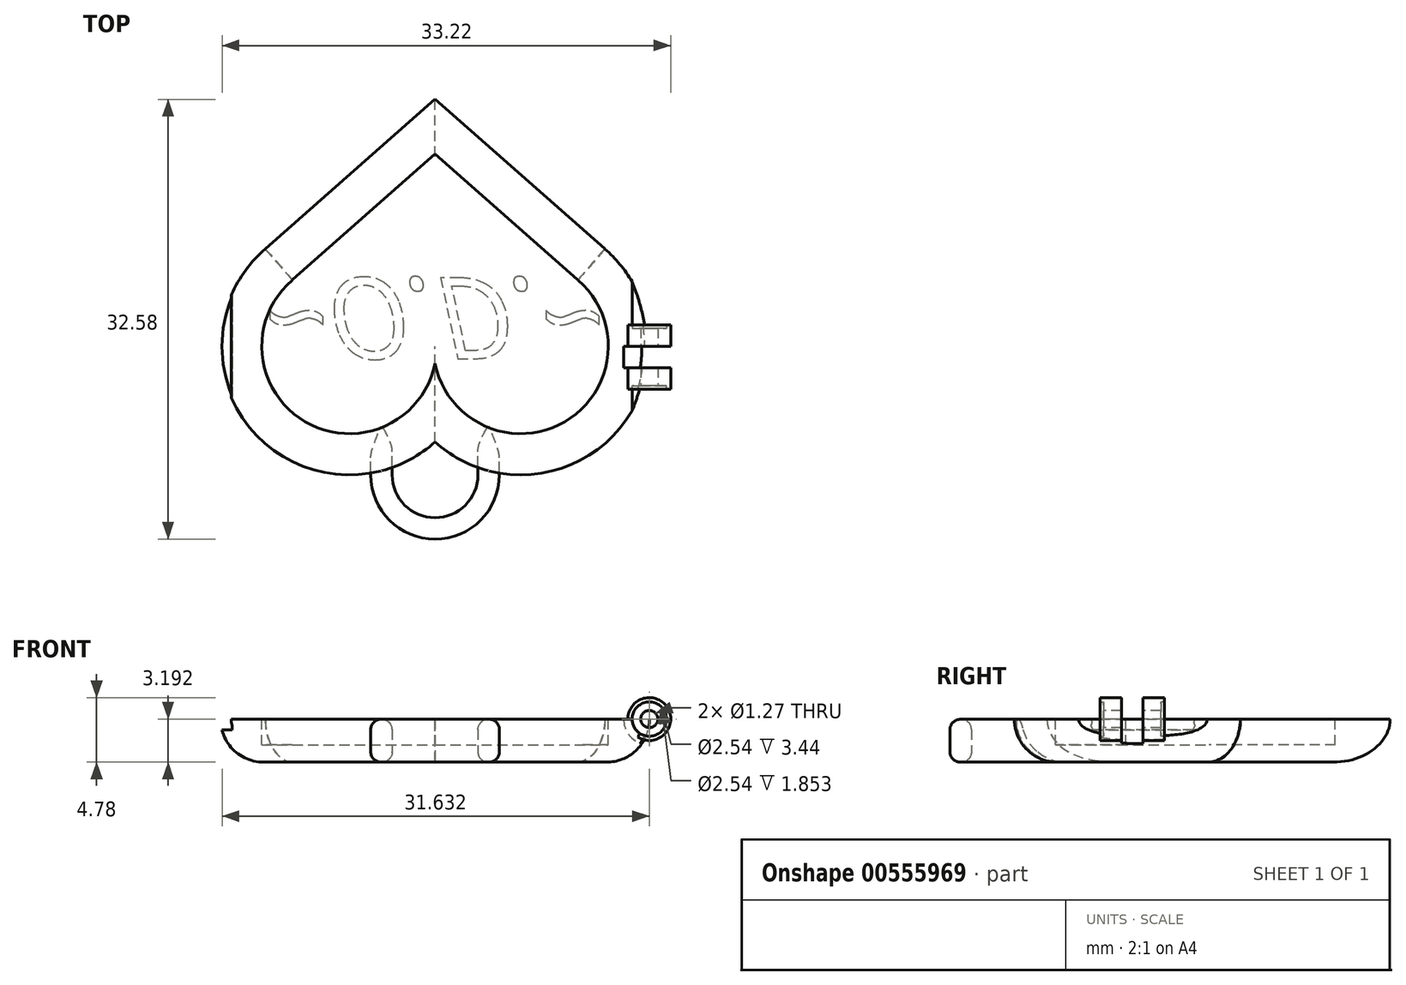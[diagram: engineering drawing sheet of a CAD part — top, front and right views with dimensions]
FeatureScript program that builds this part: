
annotation { "Feature Type Name" : "Feature", "Feature Type Description" : "" }
export const myFeature = defineFeature(function(context is Context, id is Id, definition is map)
    precondition{}
    {
        {
            var Q0;
            Q0=qCreatedBy(makeId("Top.planeOp"),FACE);
            var sketch = newSketch(context, id + "F0", { "sketchPlane" : qUnion([Q0])});
            skArc(sketch, "E0", {"start": v(0, 7.1) * mm, "mid": v(-13.5, 6.29) * mm, "end": v(-12.57, -7.21) * mm});
            skArc(sketch, "E1", {"start": v(0, 7.1) * mm, "mid": v(13.5, 6.29) * mm, "end": v(12.57, -7.21) * mm});
            skLineSegment(sketch, "E2", {"start": v(-12.57, -7.21) * mm, "end": v(0, -18.3) * mm});
            skLineSegment(sketch, "E3", {"start": v(0, -18.3) * mm, "end": v(12.57, -7.21) * mm});
            skSolve(sketch);
        }
        {
            var Q0;
            Q0=makeQuery(id+"F0.imprint","IMPRINT",FACE,{"disambiguationData":[TD([[makeQuery(id+"F0.imprint","IMPRINT",EDGE,{"derivedFrom":sQuery(id+"F0.wireOp",EDGE,"E0")}),1.0]])]});
            extrude(context, id + "F1", {"entities" : qUnion([Q0]), "depth" : 6.35 * mm});
        }
        {
            var Q0;
            Q0=makeQuery(id+"F1.opExtrude","CAP_FACE",FACE,{"disambiguationData":[OSD([sQuery(id+"F0.wireOp",EDGE,"E0"),sQuery(id+"F0.wireOp",EDGE,"E1"),sQuery(id+"F0.wireOp",EDGE,"E2"),sQuery(id+"F0.wireOp",EDGE,"E3")])],"isStart":false});
            var Q1;
            Q1=makeQuery(id+"F1.opExtrude","CAP_FACE",FACE,{"disambiguationData":[OSD([sQuery(id+"F0.wireOp",EDGE,"E0"),sQuery(id+"F0.wireOp",EDGE,"E1"),sQuery(id+"F0.wireOp",EDGE,"E2"),sQuery(id+"F0.wireOp",EDGE,"E3")])],"isStart":true});
            fillet(context, id + "F2", {"entities" : qUnion([Q0, Q1]), "radius" : 3.17 * mm, "tangentPropagation" : true, "allowEdgeOverflow" : false});
        }
        {
            var Q0;
            Q0=makeQuery(id+"F2.opFillet","BLEND_EDGE",EDGE,{"blendedFrom":[makeQuery(id+"F1.opExtrude","CAP_EDGE",EDGE,{"disambiguationData":[OSD([sQuery(id+"F0.wireOp",EDGE,"E0")])],"isStart":false}),makeQuery(id+"F1.opExtrude","CAP_EDGE",EDGE,{"disambiguationData":[OSD([sQuery(id+"F0.wireOp",EDGE,"E2")])],"isStart":false})],"blendedInto":[]});
            var Q1;
            Q1=makeQuery(id+"F2.opFillet","BLEND_EDGE",EDGE,{"blendedFrom":[makeQuery(id+"F1.opExtrude","CAP_EDGE",EDGE,{"disambiguationData":[OSD([sQuery(id+"F0.wireOp",EDGE,"E1")])],"isStart":false}),makeQuery(id+"F1.opExtrude","CAP_EDGE",EDGE,{"disambiguationData":[OSD([sQuery(id+"F0.wireOp",EDGE,"E3")])],"isStart":false})],"blendedInto":[]});
            fillet(context, id + "F3", {"entities" : qUnion([Q0, Q1]), "radius" : 2.54 * mm, "tangentPropagation" : true, "allowEdgeOverflow" : false});
        }
        {
            var Q0;
            Q0=qCreatedBy(makeId("Top.planeOp"),FACE);
            var sketch = newSketch(context, id + "F4", { "sketchPlane" : qUnion([Q0])});
            skCircle(sketch, "E4", {"center": v(0, 9.53) * mm, "radius": 3.18 * mm});
            skCircle(sketch, "E5", {"center": v(0, 9.53) * mm, "radius": 4.76 * mm});
            skLineSegment(sketch, "E6", {"start": v(-4.76, 9.53) * mm, "end": v(-4.76, 0) * mm});
            skLineSegment(sketch, "E7", {"start": v(4.76, 9.53) * mm, "end": v(4.76, 0) * mm});
            skLineSegment(sketch, "E8", {"start": v(3.18, 9.53) * mm, "end": v(3.18, 0) * mm});
            skLineSegment(sketch, "E9", {"start": v(-3.17, 9.53) * mm, "end": v(-3.17, 0) * mm});
            skLineSegment(sketch, "E10", {"start": v(-4.76, 0) * mm, "end": v(4.76, 0) * mm});
            skSolve(sketch);
        }
        {
            var Q0;
            {var subQ5=sQuery(id+"F4.wireOp",EDGE,"E8");var subQ7=sQuery(id+"F4.wireOp",EDGE,"E4");var subQ8=makeQuery(id+"F4.imprint","INTERSECT",VERTEX,{"derivedFrom":[subQ7,subQ5]});Q0=makeQuery(id+"F4.imprint","IMPRINT",FACE,{"disambiguationData":[TD([[makeQuery(id+"F4.imprint","IMPRINT",EDGE,{"disambiguationData":[TD([[subQ8,-1.0]])],"derivedFrom":subQ7}),-1.0]])]});}
            var Q1;
            {var subQ0=sQuery(id+"F4.wireOp",EDGE,"E7");Q1=makeQuery(id+"F4.imprint","IMPRINT",FACE,{"disambiguationData":[TD([[makeQuery(id+"F4.imprint","IMPRINT",EDGE,{"derivedFrom":subQ0}),-1.0]])]});}
            var Q2;
            {var subQ0=sQuery(id+"F4.wireOp",EDGE,"E6");Q2=makeQuery(id+"F4.imprint","IMPRINT",FACE,{"disambiguationData":[TD([[makeQuery(id+"F4.imprint","IMPRINT",EDGE,{"derivedFrom":subQ0}),1.0]])]});}
            extrude(context, id + "F5", {"entities" : qUnion([Q0, Q1, Q2]), "operationType" : NewBodyOperationType.ADD, "depth" : 3.17 * mm});
        }
        {
            var Q0;
            Q0=makeQuery(id+"F5.opExtrude","CAP_EDGE",EDGE,{"disambiguationData":[OSD([sQuery(id+"F4.wireOp",EDGE,"E4")])],"isStart":true});
            var Q1;
            Q1=makeQuery(id+"F5.opExtrude","CAP_EDGE",EDGE,{"disambiguationData":[OSD([sQuery(id+"F4.wireOp",EDGE,"E5")])],"isStart":true});
            var Q2;
            Q2=makeQuery(id+"F5.opExtrude","CAP_EDGE",EDGE,{"disambiguationData":[OSD([sQuery(id+"F4.wireOp",EDGE,"E5")])],"isStart":false});
            var Q3;
            Q3=makeQuery(id+"F5.opExtrude","CAP_EDGE",EDGE,{"disambiguationData":[OSD([sQuery(id+"F4.wireOp",EDGE,"E4")])],"isStart":false});
            fillet(context, id + "F6", {"entities" : qUnion([Q0, Q1, Q2, Q3]), "radius" : 0.76 * mm, "tangentPropagation" : true, "allowEdgeOverflow" : false});
        }
        {
            var Q0;
            Q0=qCreatedBy(makeId("Front.planeOp"),FACE);
            var sketch = newSketch(context, id + "F7", { "sketchPlane" : qUnion([Q0])});
            skLineSegment(sketch, "E11.bottom", {"start": v(18.97, 3.18) * mm, "end": v(-18.97, 3.18) * mm});
            skLineSegment(sketch, "E11.top", {"start": v(18.97, 9.53) * mm, "end": v(-18.97, 9.53) * mm});
            skLineSegment(sketch, "E11.left", {"start": v(18.97, 3.18) * mm, "end": v(18.97, 9.53) * mm});
            skLineSegment(sketch, "E11.right", {"start": v(-18.97, 3.18) * mm, "end": v(-18.97, 9.53) * mm});
            skPoint(sketch, "E11.middle", {"position": v(0, 6.35) * mm});
            skSolve(sketch);
        }
        {
            var Q0;
            Q0=qSketchRegion(id+"F7",true);
            extrude(context, id + "F8", {"entities" : qUnion([Q0]), "operationType" : NewBodyOperationType.REMOVE, "endBound" : BoundingType.SYMMETRIC, "oppositeDirection" : true, "depth" : 50.8 * mm});
        }
        {
            var Q0;
            Q0=makeQuery(id+"F8.boolean.opBoolean","MERGE",FACE,{"derivedFrom":[makeQuery(id+"F5.opExtrude","CAP_FACE",FACE,{"disambiguationData":[OSD([sQuery(id+"F4.wireOp",EDGE,"E4"),sQuery(id+"F4.wireOp",EDGE,"E5"),sQuery(id+"F4.wireOp",EDGE,"E6"),sQuery(id+"F4.wireOp",EDGE,"E7"),sQuery(id+"F4.wireOp",EDGE,"E8"),sQuery(id+"F4.wireOp",EDGE,"E9"),sQuery(id+"F4.wireOp",EDGE,"E10")])],"isStart":false}),makeQuery(id+"F8.opExtrude","SWEPT_FACE",FACE,{"disambiguationData":[OSD([sQuery(id+"F7.wireOp",EDGE,"E11.bottom")])]})]});
            shell(context, id + "F9", {"entities" : qUnion([Q0]), "thickness" : 3.05 * mm});
        }
        {
            var Q0;
            Q0=makeQuery(id+"F8.boolean.opBoolean","MERGE",FACE,{"derivedFrom":[makeQuery(id+"F5.opExtrude","CAP_FACE",FACE,{"disambiguationData":[OSD([sQuery(id+"F4.wireOp",EDGE,"E4"),sQuery(id+"F4.wireOp",EDGE,"E5"),sQuery(id+"F4.wireOp",EDGE,"E6"),sQuery(id+"F4.wireOp",EDGE,"E7"),sQuery(id+"F4.wireOp",EDGE,"E8"),sQuery(id+"F4.wireOp",EDGE,"E9"),sQuery(id+"F4.wireOp",EDGE,"E10")])],"isStart":false}),makeQuery(id+"F8.opExtrude","SWEPT_FACE",FACE,{"disambiguationData":[OSD([sQuery(id+"F7.wireOp",EDGE,"E11.bottom")])]})]});
            var sketch = newSketch(context, id + "F10", { "sketchPlane" : qUnion([Q0])});
            skLineSegment(sketch, "E12", {"start": v(0, -14.24) * mm, "end": v(10.55, -4.93) * mm});
            skLineSegment(sketch, "E13", {"start": v(0, -14.24) * mm, "end": v(-10.55, -4.93) * mm});
            skArc(sketch, "E14", {"start": v(0, 1.28) * mm, "mid": v(-9.61, 5.6) * mm, "end": v(-10.59, -4.9) * mm});
            skArc(sketch, "E15", {"start": v(0, 1.28) * mm, "mid": v(9.61, 5.6) * mm, "end": v(10.59, -4.9) * mm});
            skLineSegment(sketch, "E16", {"start": v(10.55, -4.93) * mm, "end": v(10.59, -4.9) * mm});
            skLineSegment(sketch, "E17", {"start": v(-10.59, -4.9) * mm, "end": v(-10.55, -4.93) * mm});
            skSolve(sketch);
        }
        {
            var Q0;
            Q0=qSketchRegion(id+"F10",true);
            extrude(context, id + "F11", {"entities" : qUnion([Q0]), "operationType" : NewBodyOperationType.REMOVE, "oppositeDirection" : true, "depth" : 1.9 * mm});
        }
        {
            var Q0;
            Q0=qCreatedBy(makeId("Front.planeOp"),FACE);
            var sketch = newSketch(context, id + "F12", { "sketchPlane" : qUnion([Q0])});
            skCircle(sketch, "E18", {"center": v(-15.86, 3.2) * mm, "radius": 1.59 * mm});
            skCircle(sketch, "E19", {"center": v(-15.86, 3.2) * mm, "radius": 0.64 * mm});
            skSolve(sketch);
        }
        {
            var Q0;
            Q0=qSketchRegion(id+"F12",true);
            extrude(context, id + "F13", {"entities" : qUnion([Q0]), "operationType" : NewBodyOperationType.ADD, "depth" : 1.59 * mm});
        }
        {
            var Q0;
            Q0=qSketchRegion(id+"F12",true);
            extrude(context, id + "F14", {"entities" : qUnion([Q0]), "operationType" : NewBodyOperationType.ADD, "oppositeDirection" : true, "depth" : 3.17 * mm, "hasSecondDirection" : true, "secondDirectionOppositeDirection" : true, "secondDirectionDepth" : 1.59 * mm});
        }
        {
            var Q0;
            Q0=makeQuery(id+"F12.imprint","IMPRINT",FACE,{"disambiguationData":[TD([[makeQuery(id+"F12.imprint","IMPRINT",EDGE,{"derivedFrom":sQuery(id+"F12.wireOp",EDGE,"E19")}),1.0]])]});
            extrude(context, id + "F15", {"entities" : qUnion([Q0]), "operationType" : NewBodyOperationType.REMOVE, "endBound" : BoundingType.SYMMETRIC, "oppositeDirection" : true, "depth" : 25.4 * mm});
        }
        {
            var Q0;
            Q0=makeQuery(id+"F13.opExtrude","CAP_FACE",FACE,{"disambiguationData":[OSD([sQuery(id+"F12.wireOp",EDGE,"E18"),sQuery(id+"F12.wireOp",EDGE,"E19")])],"isStart":false});
            var sketch = newSketch(context, id + "F16", { "sketchPlane" : qUnion([Q0])});
            skCircle(sketch, "E20", {"center": v(-15.86, 3.2) * mm, "radius": 1.27 * mm});
            skSolve(sketch);
        }
        {
            var Q0;
            Q0=qSketchRegion(id+"F16",true);
            extrude(context, id + "F17", {"entities" : qUnion([Q0]), "operationType" : NewBodyOperationType.REMOVE, "depth" : 25.4 * mm, "hasSecondDirection" : true, "secondDirectionOppositeDirection" : true, "secondDirectionDepth" : 0.25 * mm});
        }
        {
            var Q0;
            Q0=makeQuery(id+"F14.opExtrude","CAP_FACE",FACE,{"disambiguationData":[OSD([sQuery(id+"F12.wireOp",EDGE,"E18"),sQuery(id+"F12.wireOp",EDGE,"E19")])],"isStart":false});
            var sketch = newSketch(context, id + "F18", { "sketchPlane" : qUnion([Q0])});
            skCircle(sketch, "E21", {"center": v(15.86, 3.2) * mm, "radius": 1.27 * mm});
            skSolve(sketch);
        }
        {
            var Q0;
            Q0=qSketchRegion(id+"F18",true);
            extrude(context, id + "F19", {"entities" : qUnion([Q0]), "operationType" : NewBodyOperationType.REMOVE, "depth" : 25.4 * mm, "hasSecondDirection" : true, "secondDirectionOppositeDirection" : true, "secondDirectionDepth" : 0.25 * mm});
        }
        {
            var Q0;
            Q0=makeQuery(id+"F12.imprint","IMPRINT",FACE,{"disambiguationData":[TD([[makeQuery(id+"F12.imprint","IMPRINT",EDGE,{"derivedFrom":sQuery(id+"F12.wireOp",EDGE,"E18")}),1.0]])]});
            extrude(context, id + "F20", {"entities" : qUnion([Q0]), "operationType" : NewBodyOperationType.REMOVE, "oppositeDirection" : true, "depth" : 1.59 * mm});
        }
        {
            var Q0;
            {var subQ0=sQuery(id+"F12.wireOp",EDGE,"E19");var subQ1=sQuery(id+"F12.wireOp",EDGE,"E18");Q0=makeQuery(id+"F20.boolean.opBoolean","MERGE",FACE,{"derivedFrom":[makeQuery(id+"F14.opExtrude","CAP_FACE",FACE,{"disambiguationData":[OSD([subQ1,subQ0])],"isStart":true}),makeQuery(id+"F20.opExtrude","CAP_FACE",FACE,{"disambiguationData":[OSD([subQ1,subQ0])],"isStart":false})]});}
            var sketch = newSketch(context, id + "F21", { "sketchPlane" : qUnion([Q0])});
            skCircle(sketch, "E22", {"center": v(-15.86, 3.2) * mm, "radius": 1.9 * mm});
            skSolve(sketch);
        }
        {
            var Q0;
            Q0=qSketchRegion(id+"F21",true);
            extrude(context, id + "F22", {"entities" : qUnion([Q0]), "operationType" : NewBodyOperationType.REMOVE, "depth" : 1.59 * mm});
        }
        {
            var Q0;
            Q0=qCreatedBy(makeId("Front.planeOp"),FACE);
            var sketch = newSketch(context, id + "F23", { "sketchPlane" : qUnion([Q0])});
            skLineSegment(sketch, "E23.bottom", {"start": v(15.08, 2.38) * mm, "end": v(16.67, 2.38) * mm});
            skLineSegment(sketch, "E23.top", {"start": v(15.08, 3.97) * mm, "end": v(16.67, 3.97) * mm});
            skLineSegment(sketch, "E23.left", {"start": v(15.08, 2.38) * mm, "end": v(15.08, 3.97) * mm});
            skLineSegment(sketch, "E23.right", {"start": v(16.67, 2.38) * mm, "end": v(16.67, 3.97) * mm});
            skPoint(sketch, "E23.middle", {"position": v(15.88, 3.18) * mm});
            skSolve(sketch);
        }
        {
            var Q0;
            Q0=qSketchRegion(id+"F23",true);
            extrude(context, id + "F24", {"entities" : qUnion([Q0]), "operationType" : NewBodyOperationType.REMOVE, "endBound" : BoundingType.SYMMETRIC, "oppositeDirection" : true, "depth" : 25.4 * mm});
        }
        {
            var Q0;
            Q0=makeQuery(id+"F24.boolean.opBoolean","COPY",FACE,{"derivedFrom":makeQuery(id+"F24.opExtrude","SWEPT_FACE",FACE,{"disambiguationData":[OSD([sQuery(id+"F23.wireOp",EDGE,"E23.left")])]})});
            var sketch = newSketch(context, id + "F25", { "sketchPlane" : qUnion([Q0])});
            skLineSegment(sketch, "E24.bottom", {"start": v(-3.98, 2.38) * mm, "end": v(4.4, 2.38) * mm});
            skLineSegment(sketch, "E24.top", {"start": v(-3.98, 2.78) * mm, "end": v(4.4, 2.78) * mm});
            skLineSegment(sketch, "E24.left", {"start": v(-3.98, 2.38) * mm, "end": v(-3.98, 2.78) * mm});
            skLineSegment(sketch, "E24.right", {"start": v(4.4, 2.38) * mm, "end": v(4.4, 2.78) * mm});
            skSolve(sketch);
        }
        {
            var Q0;
            Q0=qSketchRegion(id+"F25",true);
            extrude(context, id + "F26", {"entities" : qUnion([Q0]), "operationType" : NewBodyOperationType.REMOVE, "oppositeDirection" : true, "depth" : 0.06 * mm});
        }
        {
            var Q0;
            Q0=makeQuery(id+"F26.boolean.opBoolean","COPY",EDGE,{"derivedFrom":makeQuery(id+"F26.opExtrude","CAP_EDGE",EDGE,{"disambiguationData":[OSD([sQuery(id+"F25.wireOp",EDGE,"E24.top")])],"isStart":false})});
            fillet(context, id + "F27", {"entities" : qUnion([Q0]), "radius" : 0.06 * mm, "tangentPropagation" : true, "allowEdgeOverflow" : false});
        }
        {
            var Q0;
            Q0=makeQuery(id+"F27.opFillet","BLEND_EDGE",EDGE,{"blendedFrom":[makeQuery(id+"F26.boolean.opBoolean","COPY",EDGE,{"derivedFrom":makeQuery(id+"F26.opExtrude","CAP_EDGE",EDGE,{"disambiguationData":[OSD([sQuery(id+"F25.wireOp",EDGE,"E24.top")])],"isStart":false})}),makeQuery(id+"F24.boolean.opBoolean","COPY",FACE,{"derivedFrom":makeQuery(id+"F24.opExtrude","SWEPT_FACE",FACE,{"disambiguationData":[OSD([sQuery(id+"F23.wireOp",EDGE,"E23.left")])]})})],"blendedInto":[makeQuery(id+"F24.boolean.opBoolean","COPY",FACE,{"derivedFrom":makeQuery(id+"F24.opExtrude","SWEPT_FACE",FACE,{"disambiguationData":[OSD([sQuery(id+"F23.wireOp",EDGE,"E23.left")])]})})]});
            fillet(context, id + "F28", {"entities" : qUnion([Q0]), "radius" : 0.64 * mm, "tangentPropagation" : true, "allowEdgeOverflow" : false});
        }
        {
            var Q0;
            Q0=makeQuery(id+"F5.boolean.opBoolean","MERGE",FACE,{"derivedFrom":[makeQuery(id+"F1.opExtrude","CAP_FACE",FACE,{"disambiguationData":[OSD([sQuery(id+"F0.wireOp",EDGE,"E0"),sQuery(id+"F0.wireOp",EDGE,"E1"),sQuery(id+"F0.wireOp",EDGE,"E2"),sQuery(id+"F0.wireOp",EDGE,"E3")])],"isStart":true}),makeQuery(id+"F5.opExtrude","CAP_FACE",FACE,{"disambiguationData":[OSD([sQuery(id+"F4.wireOp",EDGE,"E4"),sQuery(id+"F4.wireOp",EDGE,"E5"),sQuery(id+"F4.wireOp",EDGE,"E6"),sQuery(id+"F4.wireOp",EDGE,"E7"),sQuery(id+"F4.wireOp",EDGE,"E8"),sQuery(id+"F4.wireOp",EDGE,"E9"),sQuery(id+"F4.wireOp",EDGE,"E10")])],"isStart":true})]});
            var sketch = newSketch(context, id + "F29", { "sketchPlane" : qUnion([Q0])});
            skText(sketch, "E25", { "text": "~O.D.~", "fontName": "OpenSans-Italic.ttf"});
            const initialGuessF29  = {"E25": [-0.0127, 0, 1, 0, 0.00603]};
            skSetInitialGuess(sketch, initialGuessF29);
            skSolve(sketch);
        }
        {
            var Q0;
            Q0=makeQuery(id+"F1.opExtrude","SWEPT_BODY",BODY,{"disambiguationData":[OSD([sQuery(id+"F0.wireOp",EDGE,"E0"),sQuery(id+"F0.wireOp",EDGE,"E1"),sQuery(id+"F0.wireOp",EDGE,"E2"),sQuery(id+"F0.wireOp",EDGE,"E3")])]});
            var Q1;
            Q1=makeQuery(id+"F11.boolean.opBoolean","COPY",EDGE,{"derivedFrom":makeQuery(id+"F11.opExtrude","SWEPT_EDGE",EDGE,{"disambiguationData":[OSD([sQuery(id+"F10.wireOp",EDGE,"E14"),sQuery(id+"F10.wireOp",EDGE,"E15")])]})});
            transform(context, id + "F30", {"entities" : qUnion([Q0]), "transformType" : TransformType.ROTATION, "transformAxis" : qUnion([Q1]), "angle" : 180 * degree, "makeCopy" : false});
        }
        {
            var Q0;
            Q0=makeQuery(id+"F1.opExtrude","SWEPT_BODY",BODY,{"disambiguationData":[OSD([sQuery(id+"F0.wireOp",EDGE,"E0"),sQuery(id+"F0.wireOp",EDGE,"E1"),sQuery(id+"F0.wireOp",EDGE,"E2"),sQuery(id+"F0.wireOp",EDGE,"E3")])]});
            var Q1;
            Q1=qCreatedBy(makeId("Front.planeOp"),FACE);
            transform(context, id + "F31", {"entities" : qUnion([Q0]), "transformType" : TransformType.TRANSLATION_DISTANCE, "transformDirection" : qUnion([Q1]), "distance" : 7.62 * mm, "makeCopy" : false});
        }
        {
            var Q0;
            Q0 = qSketchRegion(id + "F29", true);
            extrude(context, id + "F32", {"entities" : qUnion([Q0]), "operationType" : NewBodyOperationType.REMOVE, "oppositeDirection" : true, "depth" : 0.06 / 50.8 * mm, "offsetDistance" : 25.4 * mm});
        }
    });
